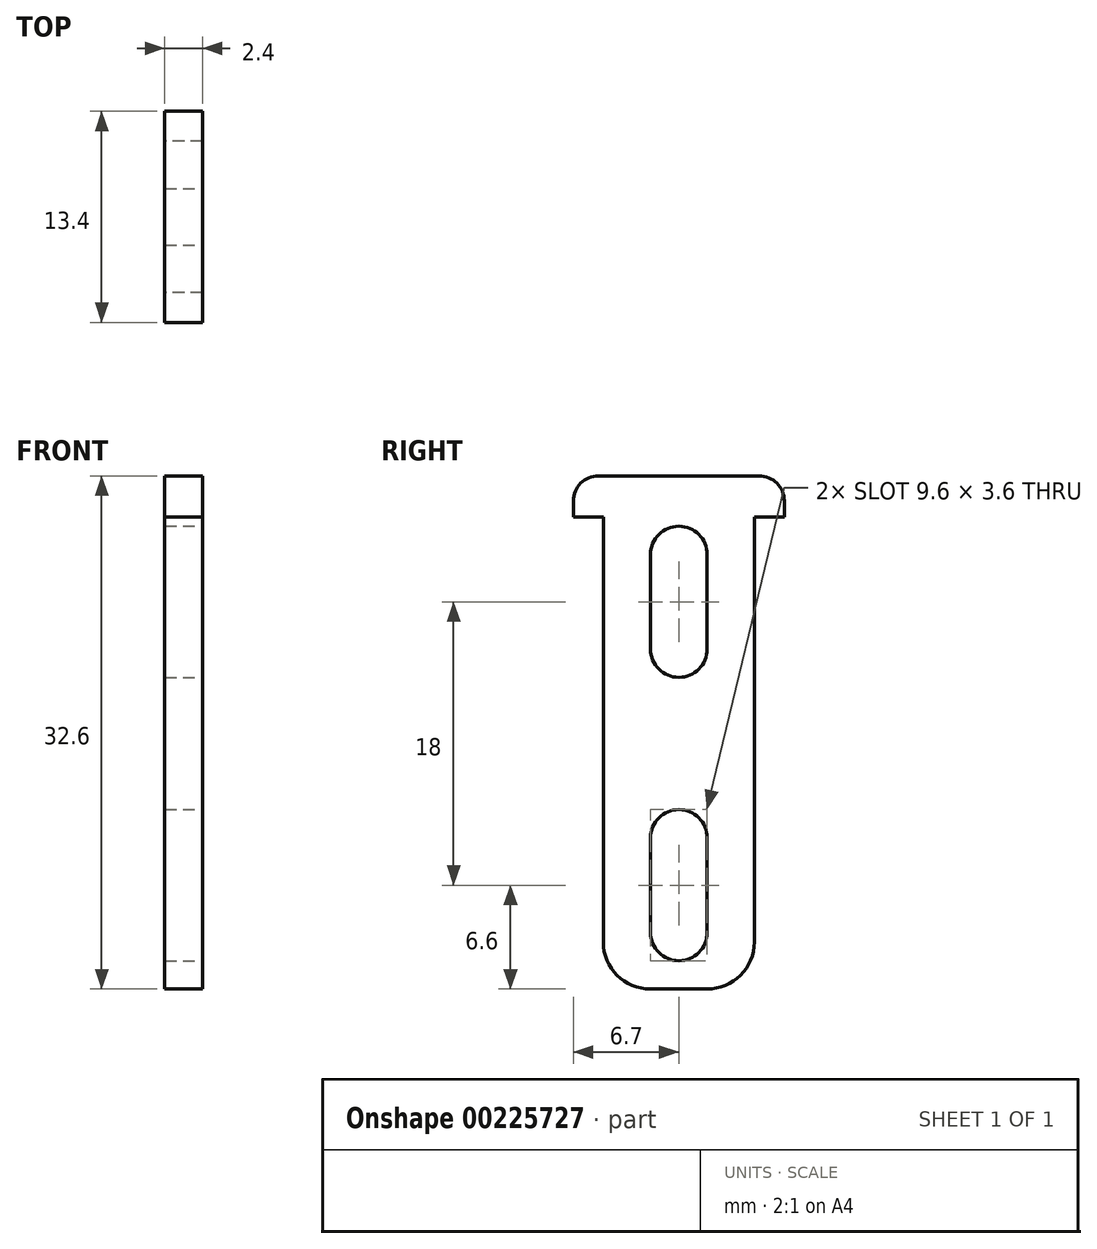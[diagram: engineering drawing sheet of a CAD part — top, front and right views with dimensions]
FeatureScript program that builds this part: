
annotation { "Feature Type Name" : "Feature", "Feature Type Description" : "" }
export const myFeature = defineFeature(function(context is Context, id is Id, definition is map)
    precondition{}
    {
        {
            var Q0;
            Q0=qCreatedBy(makeId("Right.planeOp"),FACE);
            var sketch = newSketch(context, id + "F0", { "sketchPlane" : qUnion([Q0])});
            skLineSegment(sketch, "E0", {"start": v(-6.7, 3.6) * mm, "end": v(-6.7, 1) * mm});
            skLineSegment(sketch, "E1", {"start": v(-6.7, 1) * mm, "end": v(-4.8, 1) * mm});
            skLineSegment(sketch, "E2", {"start": v(-4.8, 1) * mm, "end": v(-4.8, -29) * mm});
            skLineSegment(sketch, "E3", {"start": v(-4.8, -29) * mm, "end": v(4.8, -29) * mm});
            skLineSegment(sketch, "E4", {"start": v(4.8, -29) * mm, "end": v(4.8, 1) * mm});
            skLineSegment(sketch, "E5", {"start": v(4.8, 1) * mm, "end": v(6.7, 1) * mm});
            skLineSegment(sketch, "E6", {"start": v(6.7, 1) * mm, "end": v(6.7, 3.6) * mm});
            skLineSegment(sketch, "E7", {"start": v(6.7, 3.6) * mm, "end": v(-6.7, 3.6) * mm});
            skLineSegment(sketch, "E8", {"start": v(0, 0) * mm, "end": v(0, 3.6) * mm, "construction": true});
            skSolve(sketch);
        }
        {
            var Q0;
            Q0=qCreatedBy(makeId("Right.planeOp"),FACE);
            var sketch = newSketch(context, id + "F1", { "sketchPlane" : qUnion([Q0])});
            skLineSegment(sketch, "E9", {"start": v(0, 0) * mm, "end": v(0, -32.86) * mm, "construction": true});
            skArc(sketch, "E10", {"start": v(1.8, -1.4) * mm, "mid": v(0, 0.4) * mm, "end": v(-1.8, -1.4) * mm});
            skArc(sketch, "E11", {"start": v(-1.8, -7.4) * mm, "mid": v(0, -9.2) * mm, "end": v(1.8, -7.4) * mm});
            skArc(sketch, "E12", {"start": v(1.8, -19.4) * mm, "mid": v(0, -17.6) * mm, "end": v(-1.8, -19.4) * mm});
            skArc(sketch, "E13", {"start": v(-1.8, -25.4) * mm, "mid": v(0, -27.2) * mm, "end": v(1.8, -25.4) * mm});
            skLineSegment(sketch, "E14", {"start": v(-1.8, -1.4) * mm, "end": v(-1.8, -7.4) * mm});
            skLineSegment(sketch, "E15", {"start": v(-1.8, -19.4) * mm, "end": v(-1.8, -25.4) * mm});
            skLineSegment(sketch, "E16", {"start": v(1.8, -25.4) * mm, "end": v(1.8, -19.4) * mm});
            skLineSegment(sketch, "E17", {"start": v(1.8, -7.4) * mm, "end": v(1.8, -1.4) * mm});
            skSolve(sketch);
        }
        {
            var Q0;
            Q0=qSketchRegion(id+"F0",true);
            extrude(context, id + "F2", {"entities" : qUnion([Q0]), "endBound" : BoundingType.SYMMETRIC, "depth" : 2.4 * mm});
        }
        {
            var Q0;
            Q0=qSketchRegion(id+"F1",true);
            extrude(context, id + "F3", {"entities" : qUnion([Q0]), "operationType" : NewBodyOperationType.REMOVE, "endBound" : BoundingType.THROUGH_ALL, "oppositeDirection" : true, "depth" : 25 * mm, "hasSecondDirection" : true, "secondDirectionBound" : SecondDirectionBoundingType.THROUGH_ALL, "secondDirectionOppositeDirection" : false, "secondDirectionDepth" : 25 * mm});
        }
        {
            var Q0;
            Q0=makeQuery(id+"F2.opExtrude","SWEPT_EDGE",EDGE,{"disambiguationData":[OSD([sQuery(id+"F0.wireOp",EDGE,"E6"),sQuery(id+"F0.wireOp",EDGE,"E7")])]});
            var Q1;
            Q1=makeQuery(id+"F2.opExtrude","SWEPT_EDGE",EDGE,{"disambiguationData":[OSD([sQuery(id+"F0.wireOp",EDGE,"E0"),sQuery(id+"F0.wireOp",EDGE,"E7")])]});
            fillet(context, id + "F4", {"entities" : qUnion([Q0, Q1]), "radius" : 1.6 * mm, "tangentPropagation" : true, "allowEdgeOverflow" : false});
        }
        {
            var Q0;
            Q0=makeQuery(id+"F2.opExtrude","SWEPT_EDGE",EDGE,{"disambiguationData":[OSD([sQuery(id+"F0.wireOp",EDGE,"E3"),sQuery(id+"F0.wireOp",EDGE,"E4")])]});
            var Q1;
            Q1=makeQuery(id+"F2.opExtrude","SWEPT_EDGE",EDGE,{"disambiguationData":[OSD([sQuery(id+"F0.wireOp",EDGE,"E2"),sQuery(id+"F0.wireOp",EDGE,"E3")])]});
            fillet(context, id + "F5", {"entities" : qUnion([Q0, Q1]), "radius" : 3 * mm, "tangentPropagation" : true, "allowEdgeOverflow" : false});
        }
    });
